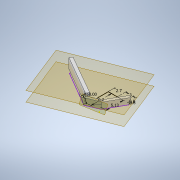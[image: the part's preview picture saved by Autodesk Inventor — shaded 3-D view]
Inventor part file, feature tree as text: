
AUTODESK INVENTOR PART (.ipt)
format: ipt  version: 2022 (Build 260153000, 153)  size: 183,296 bytes
history: native  units: in
note: dims shown in document units (in); Inventor stores cm internally (conversion verified against a paired STEP export)
features: sketch x4, plane x3, extrude x2, loft x1, split x1
ambient origin geometry x8: Origin, YZ Plane, XZ Plane, XY Plane, X Axis, Y Axis, Z Axis, Center Point
bodies: Solid1 (feature_tree)
feature tree (11):
  sketch  "Sketch1"  dims[d0=0.2441in d1=60.0deg]
  plane  "Work Plane2"
  loft  "Loft1"
  extrude  "Extrusion1"  Depth=0.202in
  extrude  "Extrusion3"  Depth=0.0315in
  sketch  "Sketch4"  dims[d8=0.0315in d11=0.1181in d14=0.0315in d15=0.0315in d16=0.0in d17=90.0deg d18=0.0in d19=90.0deg d20=0.1181in d21=0.0394in d22=0.0in d27=0.0394in d28=0.0787in d29=0.0in d30=0.0in d31=-0.0276in]
  plane  "Work Plane3"
  split  "Split3"
  plane  "Work Plane1"
  sketch  "Sketch2"  dims[d2=0.1063in d3=0.202in]
  sketch  "Sketch3"  dims[d4=0.1181in d7=0.0315in]
